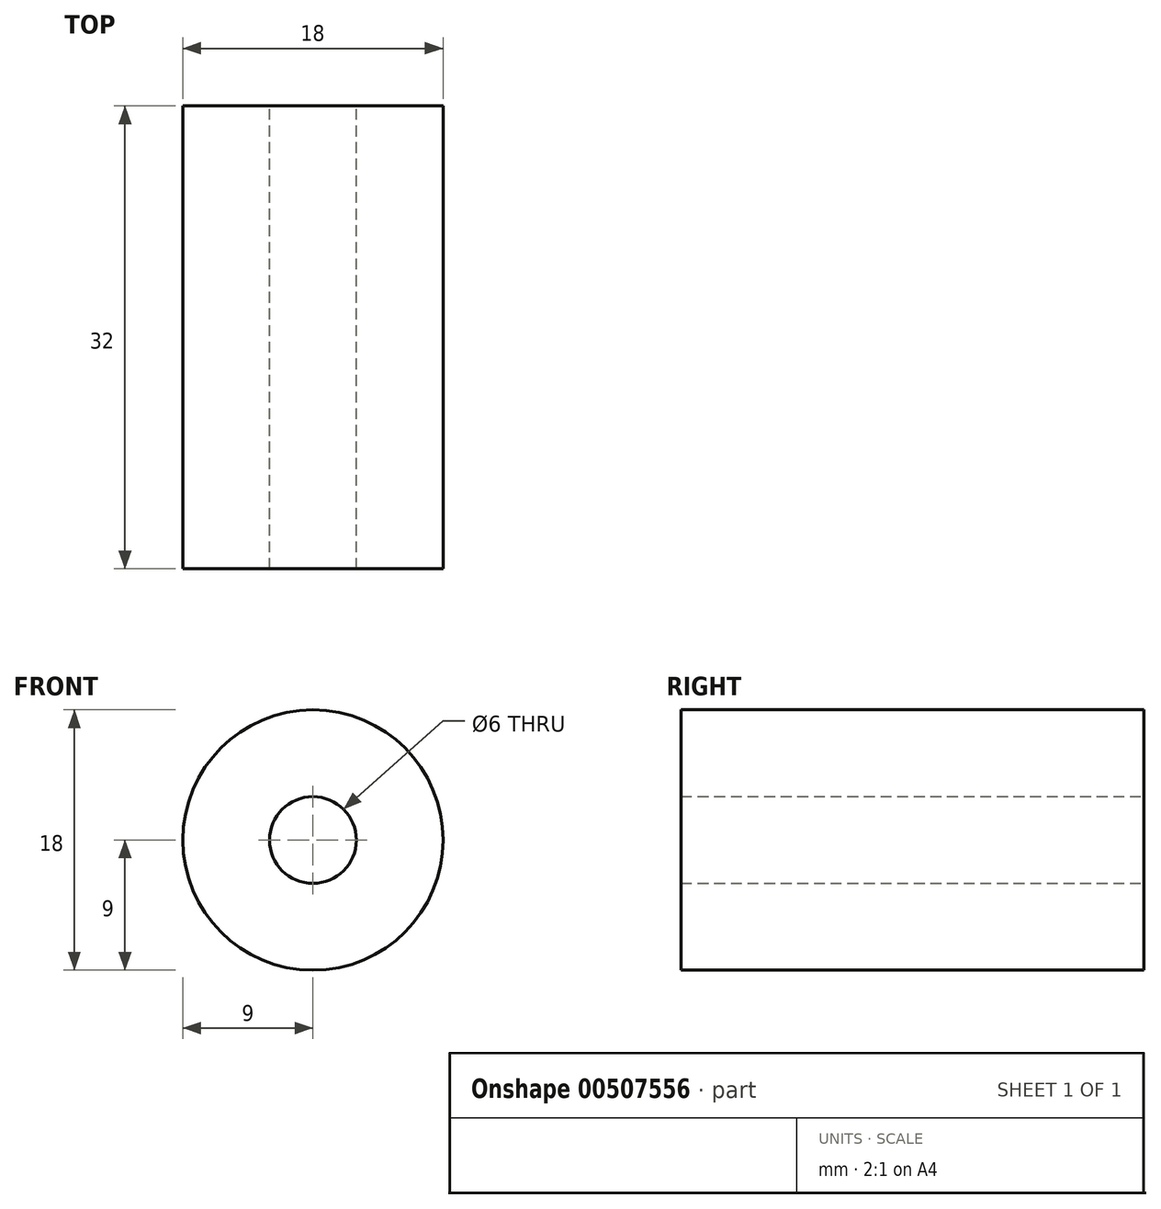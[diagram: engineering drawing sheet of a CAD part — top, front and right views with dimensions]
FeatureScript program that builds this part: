
annotation { "Feature Type Name" : "Feature", "Feature Type Description" : "" }
export const myFeature = defineFeature(function(context is Context, id is Id, definition is map)
    precondition{}
    {
        {
            var Q0;
            Q0=qCreatedBy(makeId("Front.planeOp"),FACE);
            var sketch = newSketch(context, id + "F0", { "sketchPlane" : qUnion([Q0])});
            skCircle(sketch, "E0", {"center": v(0, 0) * mm, "radius": 9 * mm});
            skCircle(sketch, "E1", {"center": v(0, 0) * mm, "radius": 3 * mm});
            skSolve(sketch);
        }
        {
            var Q0;
            Q0=makeQuery(id+"F0.imprint","IMPRINT",FACE,{"disambiguationData":[TD([[makeQuery(id+"F0.imprint","IMPRINT",EDGE,{"derivedFrom":sQuery(id+"F0.wireOp",EDGE,"E0")}),1.0]])]});
            extrude(context, id + "F1", {"entities" : qUnion([Q0]), "depth" : 32 * mm, "offsetDistance" : 25 * mm});
        }
    });
